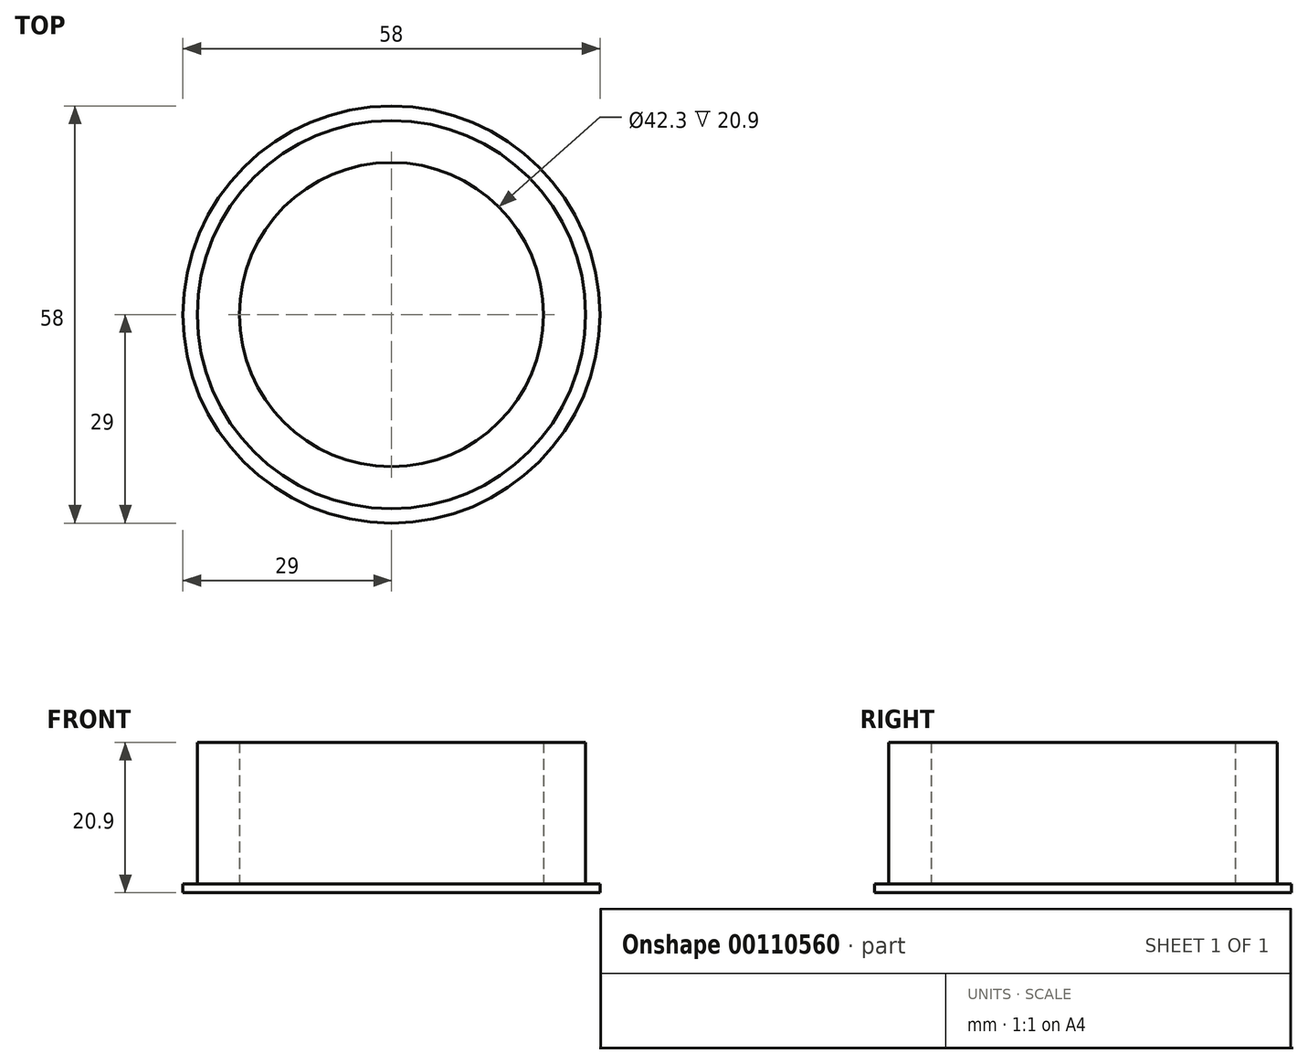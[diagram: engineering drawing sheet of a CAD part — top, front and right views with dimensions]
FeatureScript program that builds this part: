
annotation { "Feature Type Name" : "Feature", "Feature Type Description" : "" }
export const myFeature = defineFeature(function(context is Context, id is Id, definition is map)
    precondition{}
    {
        {
            var Q0;
            Q0=qCreatedBy(makeId("Top.planeOp"),FACE);
            var sketch = newSketch(context, id + "F0", { "sketchPlane" : qUnion([Q0])});
            skCircle(sketch, "E0", {"center": v(0, 0) * mm, "radius": 27 * mm});
            skCircle(sketch, "E1", {"center": v(0, 0) * mm, "radius": 21.15 * mm});
            skSolve(sketch);
        }
        {
            var Q0;
            Q0 = qSketchRegion(id + "F0", true);
            extrude(context, id + "F1", {"entities" : qUnion([Q0]), "depth" : 19.7 * mm});
        }
        {
            var Q0;
            Q0=makeQuery(id+"F1.opExtrude","CAP_FACE",FACE,{"disambiguationData":[OSD([sQuery(id+"F0.wireOp",EDGE,"E0"),sQuery(id+"F0.wireOp",EDGE,"E1")])],"isStart":true});
            var sketch = newSketch(context, id + "F2", { "sketchPlane" : qUnion([Q0])});
            skCircle(sketch, "E2.0", {"center": v(0, 0) * mm, "radius": 27 * mm, "construction": true});
            skCircle(sketch, "E3.0", {"center": v(0, 0) * mm, "radius": 29 * mm});
            skCircle(sketch, "E4.0", {"center": v(0, 0) * mm, "radius": 21.15 * mm});
            skSolve(sketch);
        }
        {
            var Q0;
            Q0 = qSketchRegion(id + "F2", true);
            extrude(context, id + "F3", {"entities" : qUnion([Q0]), "operationType" : NewBodyOperationType.ADD, "depth" : 1.2 * mm});
        }
    });
